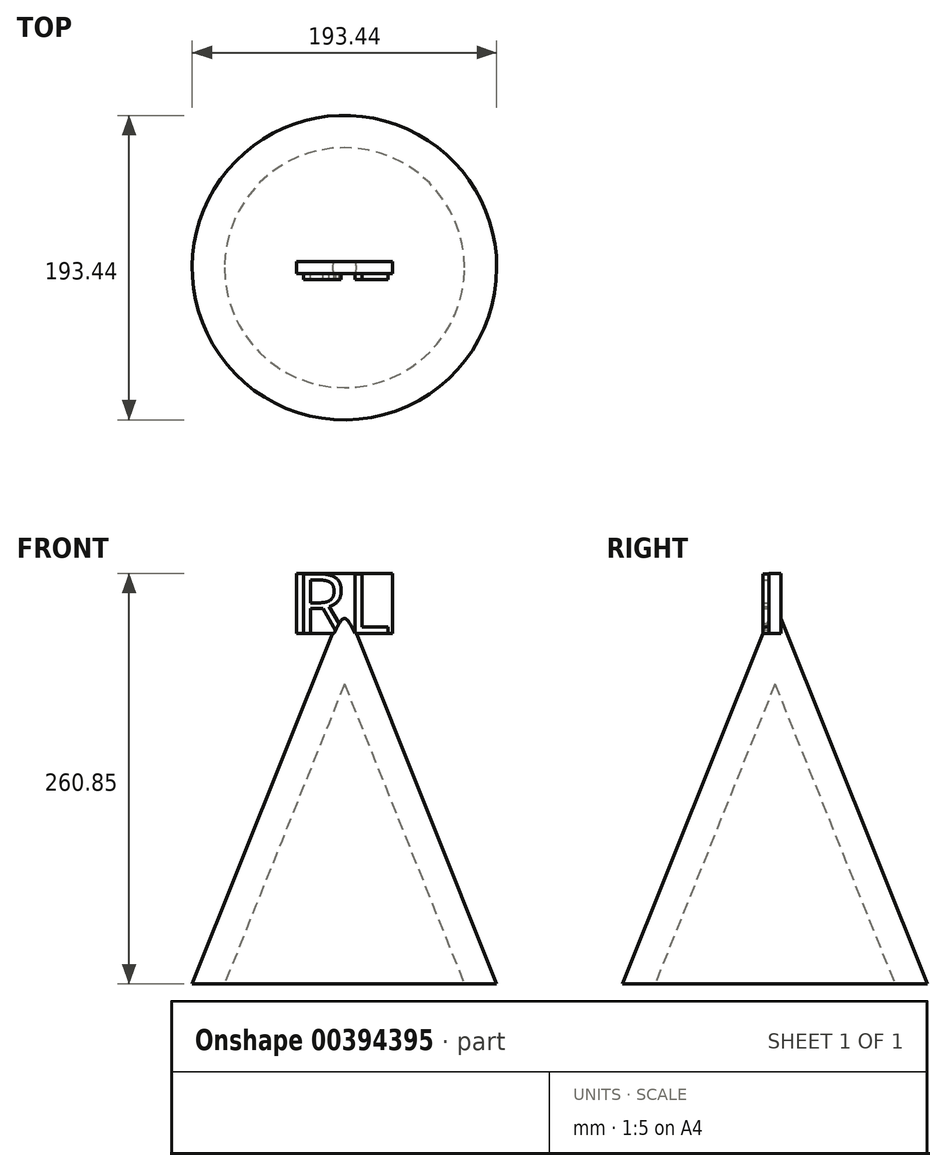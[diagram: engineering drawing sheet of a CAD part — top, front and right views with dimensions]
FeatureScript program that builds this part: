
annotation { "Feature Type Name" : "Feature", "Feature Type Description" : "" }
export const myFeature = defineFeature(function(context is Context, id is Id, definition is map)
    precondition{}
    {
        {
            var Q0;
            Q0=qCreatedBy(makeId("Front.planeOp"),FACE);
            var sketch = newSketch(context, id + "F0", { "sketchPlane" : qUnion([Q0])});
            skLineSegment(sketch, "E0", {"start": v(25.4, 0) * mm, "end": v(32.24, 0) * mm});
            skLineSegment(sketch, "E1", {"start": v(32.24, 0) * mm, "end": v(0, 80.6) * mm});
            skLineSegment(sketch, "E2", {"start": v(0, 80.6) * mm, "end": v(0, 63.5) * mm});
            skLineSegment(sketch, "E3", {"start": v(0, 63.5) * mm, "end": v(25.4, 0) * mm});
            skSolve(sketch);
        }
        {
            var Q0;
            Q0=makeQuery(id+"F0.imprint","IMPRINT",FACE,{"disambiguationData":[TD([[makeQuery(id+"F0.imprint","IMPRINT",EDGE,{"derivedFrom":sQuery(id+"F0.wireOp",EDGE,"E0")}),1.0]])]});
            var Q1;
            Q1=sQuery(id+"F0.wireOp",EDGE,"E2");
            revolve(context, id + "F1", {"entities" : qUnion([Q0]), "axis" : qUnion([Q1]), "revolveType" : RevolveType.FULL});
        }
        {
            var Q0;
            Q0=qCreatedBy(makeId("Front.planeOp"),FACE);
            var sketch = newSketch(context, id + "F2", { "sketchPlane" : qUnion([Q0])});
            skLineSegment(sketch, "E4.bottom", {"start": v(10.16, 86.95) * mm, "end": v(-10.16, 86.95) * mm});
            skLineSegment(sketch, "E4.top", {"start": v(10.16, 74.25) * mm, "end": v(-10.16, 74.25) * mm});
            skLineSegment(sketch, "E4.left", {"start": v(10.16, 86.95) * mm, "end": v(10.16, 74.25) * mm});
            skLineSegment(sketch, "E4.right", {"start": v(-10.16, 86.95) * mm, "end": v(-10.16, 74.25) * mm});
            skPoint(sketch, "E4.middle", {"position": v(0, 80.6) * mm});
            skSolve(sketch);
        }
        {
            var Q0;
            Q0=makeQuery(id+"F2.imprint","IMPRINT",FACE,{"disambiguationData":[TD([[makeQuery(id+"F2.imprint","IMPRINT",EDGE,{"derivedFrom":sQuery(id+"F2.wireOp",EDGE,"E4.bottom")}),1.0]])]});
            extrude(context, id + "F3", {"entities" : qUnion([Q0]), "operationType" : NewBodyOperationType.ADD, "endBound" : BoundingType.SYMMETRIC, "depth" : 2.54 * mm});
        }
        {
            var Q0;
            Q0=makeQuery(id+"F3.opExtrude","CAP_FACE",FACE,{"disambiguationData":[OSD([sQuery(id+"F2.wireOp",EDGE,"E4.bottom"),sQuery(id+"F2.wireOp",EDGE,"E4.top"),sQuery(id+"F2.wireOp",EDGE,"E4.left"),sQuery(id+"F2.wireOp",EDGE,"E4.right")])],"isStart":false});
            var sketch = newSketch(context, id + "F4", { "sketchPlane" : qUnion([Q0])});
            skText(sketch, "E5", { "text": "RL", "fontName": "OpenSans-Regular.ttf"});
            const initialGuessF4  = {"E5": [-0.0104, 0.07425, 1, 0, 0.0127]};
            skSetInitialGuess(sketch, initialGuessF4);
            skSolve(sketch);
        }
        {
            var Q0;
            Q0=makeQuery(id+"F4.imprint","IMPRINT",FACE,{"disambiguationData":[TD([[makeQuery(id+"F4.imprint","IMPRINT",EDGE,{"derivedFrom":sQuery(id+"F4.wireOp",EDGE,"E5.sketch_text.stroke-0")}),-1.0]])]});
            var Q1;
            Q1=makeQuery(id+"F4.imprint","IMPRINT",FACE,{"disambiguationData":[TD([[makeQuery(id+"F4.imprint","IMPRINT",EDGE,{"derivedFrom":sQuery(id+"F4.wireOp",EDGE,"E5.sketch_text.stroke-18")}),-1.0]])]});
            extrude(context, id + "F5", {"entities" : qUnion([Q0, Q1]), "operationType" : NewBodyOperationType.ADD, "depth" : 1.27 * mm});
        }
        {
            var Q0;
            Q0=makeQuery(id+"F1.opRevolve","SWEPT_BODY",BODY,{"disambiguationData":[OSD([sQuery(id+"F0.wireOp",EDGE,"E0"),sQuery(id+"F0.wireOp",EDGE,"E1"),sQuery(id+"F0.wireOp",EDGE,"E2"),sQuery(id+"F0.wireOp",EDGE,"E3")])]});
            var Q1;
            Q1=makeQuery(id+"F3.opExtrude","CAP_VERTEX",VERTEX,{"disambiguationData":[OSD([sQuery(id+"F2.wireOp",EDGE,"E4.bottom"),sQuery(id+"F2.wireOp",EDGE,"E4.right")])],"isStart":false});
            transform(context, id + "F6", {"entities" : qUnion([Q0]), "transformType" : TransformType.SCALE_UNIFORMLY, "scale" : 3, "scalePoint" : qUnion([Q1]), "makeCopy" : false});
        }
    });
